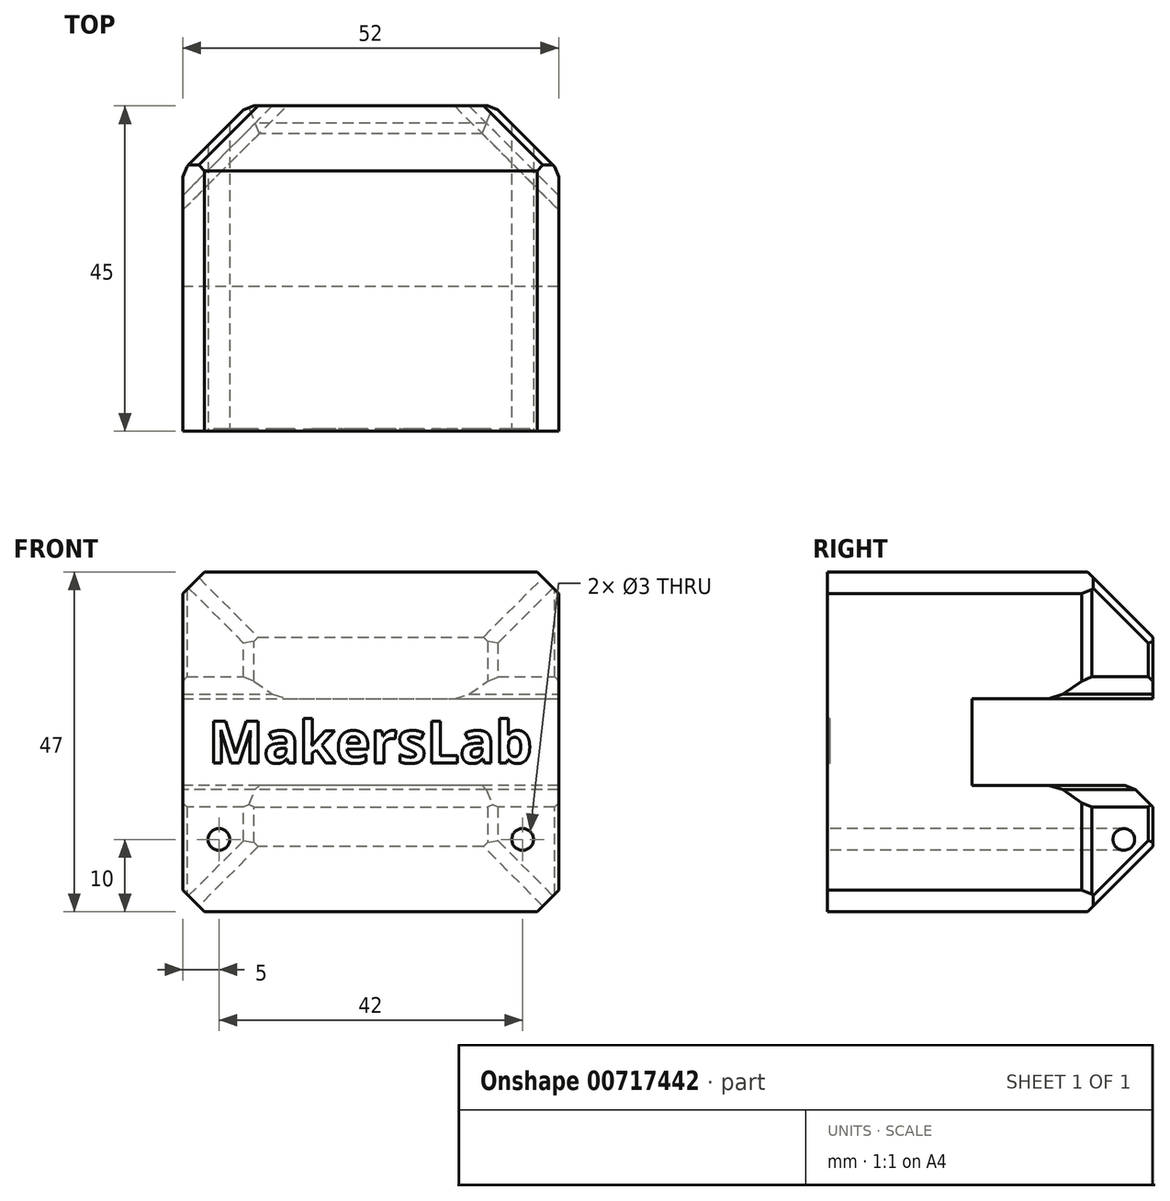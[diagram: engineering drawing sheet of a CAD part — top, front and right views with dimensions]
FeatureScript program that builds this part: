
annotation { "Feature Type Name" : "Feature", "Feature Type Description" : "" }
export const myFeature = defineFeature(function(context is Context, id is Id, definition is map)
    precondition{}
    {
        {
            var Q0;
            Q0=qCreatedBy(makeId("Front.planeOp"),FACE);
            var sketch = newSketch(context, id + "F0", { "sketchPlane" : qUnion([Q0])});
            skLineSegment(sketch, "E0", {"start": v(0, 0) * mm, "end": v(52, 0) * mm});
            skLineSegment(sketch, "E1", {"start": v(52, 0) * mm, "end": v(52, 47) * mm});
            skLineSegment(sketch, "E2", {"start": v(52, 47) * mm, "end": v(0, 47) * mm});
            skLineSegment(sketch, "E3", {"start": v(0, 47) * mm, "end": v(0, 0) * mm});
            skSolve(sketch);
        }
        {
            var Q0;
            Q0=makeQuery(id+"F0.imprint","IMPRINT",FACE,{"disambiguationData":[TD([[makeQuery(id+"F0.imprint","IMPRINT",EDGE,{"derivedFrom":sQuery(id+"F0.wireOp",EDGE,"E0")}),1.0]])]});
            extrude(context, id + "F1", {"entities" : qUnion([Q0]), "depth" : 45 * mm, "offsetDistance" : 25 * mm});
        }
        {
            var Q0;
            Q0=makeQuery(id+"F1.opExtrude","CAP_FACE",FACE,{"disambiguationData":[OSD([sQuery(id+"F0.wireOp",EDGE,"E0"),sQuery(id+"F0.wireOp",EDGE,"E1"),sQuery(id+"F0.wireOp",EDGE,"E2"),sQuery(id+"F0.wireOp",EDGE,"E3")])],"isStart":false});
            var sketch = newSketch(context, id + "F2", { "sketchPlane" : qUnion([Q0])});
            skCircle(sketch, "E4", {"center": v(5, 10) * mm, "radius": 1.5 * mm});
            skCircle(sketch, "E5", {"center": v(47, 10) * mm, "radius": 1.5 * mm});
            skSolve(sketch);
        }
        {
            var Q0;
            Q0 = qSketchRegion(id + "F2", true);
            extrude(context, id + "F3", {"entities" : qUnion([Q0]), "operationType" : NewBodyOperationType.REMOVE, "oppositeDirection" : true, "depth" : 100 * mm, "offsetDistance" : 25 * mm});
        }
        {
            var Q0;
            Q0=makeQuery(id+"F1.opExtrude","CAP_EDGE",EDGE,{"disambiguationData":[OSD([sQuery(id+"F0.wireOp",EDGE,"E0")])],"isStart":true});
            var Q1;
            Q1=makeQuery(id+"F1.opExtrude","CAP_EDGE",EDGE,{"disambiguationData":[OSD([sQuery(id+"F0.wireOp",EDGE,"E2")])],"isStart":true});
            var Q2;
            Q2=makeQuery(id+"F1.opExtrude","CAP_EDGE",EDGE,{"disambiguationData":[OSD([sQuery(id+"F0.wireOp",EDGE,"E3")])],"isStart":true});
            var Q3;
            Q3=makeQuery(id+"F1.opExtrude","CAP_EDGE",EDGE,{"disambiguationData":[OSD([sQuery(id+"F0.wireOp",EDGE,"E1")])],"isStart":true});
            chamfer(context, id + "F4", {"entities" : qUnion([Q0, Q1, Q2, Q3]), "width" : 9 * mm, "tangentPropagation" : true});
        }
        {
            var Q0;
            Q0=makeQuery(id+"F1.opExtrude","CAP_FACE",FACE,{"disambiguationData":[OSD([sQuery(id+"F0.wireOp",EDGE,"E0"),sQuery(id+"F0.wireOp",EDGE,"E1"),sQuery(id+"F0.wireOp",EDGE,"E2"),sQuery(id+"F0.wireOp",EDGE,"E3")])],"isStart":true});
            var sketch = newSketch(context, id + "F5", { "sketchPlane" : qUnion([Q0])});
            skLineSegment(sketch, "E6", {"start": v(0, 23.5) * mm, "end": v(0, 29.5) * mm});
            skPoint(sketch, "E6.startSnap0", {"position": v(-9, 23.5) * mm});
            skLineSegment(sketch, "E7", {"start": v(0, 29.5) * mm, "end": v(-52, 29.5) * mm});
            skLineSegment(sketch, "E8", {"start": v(-52, 29.5) * mm, "end": v(-52, 17.5) * mm});
            skLineSegment(sketch, "E9", {"start": v(-52, 17.5) * mm, "end": v(0, 17.5) * mm});
            skLineSegment(sketch, "E10", {"start": v(0, 17.5) * mm, "end": v(0, 23.5) * mm});
            skSolve(sketch);
        }
        {
            var Q0;
            {var subQ0=sQuery(id+"F5.wireOp",EDGE,"E7");var subQ1=sQuery(id+"F0.wireOp",EDGE,"E3");var subQ2=sQuery(id+"F0.wireOp",EDGE,"E1");var subQ3=makeQuery(id+"F1.opExtrude","CAP_FACE",FACE,{"disambiguationData":[OSD([sQuery(id+"F0.wireOp",EDGE,"E0"),subQ2,sQuery(id+"F0.wireOp",EDGE,"E2"),subQ1])],"isStart":true});var subQ4=makeQuery(id+"F4.opChamfer","BLEND_EDGE",EDGE,{"blendedFrom":[makeQuery(id+"F1.opExtrude","CAP_EDGE",EDGE,{"disambiguationData":[OSD([subQ1])],"isStart":true}),subQ3],"blendedInto":[subQ3]});var subQ5=makeQuery(id+"F5.imprint","INTERSECT",VERTEX,{"derivedFrom":[subQ4,subQ0]});Q0=makeQuery(id+"F5.imprint","IMPRINT",FACE,{"disambiguationData":[TD([[makeQuery(id+"F5.imprint","IMPRINT",EDGE,{"disambiguationData":[TD([[subQ5,-1.0]])],"derivedFrom":subQ0}),1.0]])]});}
            var Q1;
            {var subQ6=sQuery(id+"F5.wireOp",EDGE,"E6");Q1=makeQuery(id+"F5.imprint","IMPRINT",FACE,{"disambiguationData":[TD([[makeQuery(id+"F5.imprint","IMPRINT",EDGE,{"derivedFrom":subQ6}),1.0]])]});}
            var Q2;
            {var subQ0=sQuery(id+"F5.wireOp",EDGE,"E8");Q2=makeQuery(id+"F5.imprint","IMPRINT",FACE,{"disambiguationData":[TD([[makeQuery(id+"F5.imprint","IMPRINT",EDGE,{"derivedFrom":subQ0}),1.0]])]});}
            extrude(context, id + "F6", {"entities" : qUnion([Q0, Q1, Q2]), "operationType" : NewBodyOperationType.REMOVE, "oppositeDirection" : true, "depth" : 25 * mm, "offsetDistance" : 25 * mm});
        }
        {
            var Q0;
            Q0=makeQuery(id+"F6.boolean.opBoolean","INTERSECT",EDGE,{"derivedFrom":[makeQuery(id+"F4.opChamfer","BLEND_FACE",FACE,{"disambiguationData":[OSD([sQuery(id+"F0.wireOp",EDGE,"E1")])]}),makeQuery(id+"F6.opExtrude","SWEPT_FACE",FACE,{"disambiguationData":[OSD([sQuery(id+"F5.wireOp",EDGE,"E7")])]})]});
            var Q1;
            Q1=makeQuery(id+"F6.boolean.opBoolean","COPY",EDGE,{"derivedFrom":makeQuery(id+"F6.opExtrude","CAP_EDGE",EDGE,{"disambiguationData":[OSD([sQuery(id+"F5.wireOp",EDGE,"E7")])],"isStart":true})});
            var Q2;
            Q2=makeQuery(id+"F6.boolean.opBoolean","INTERSECT",EDGE,{"derivedFrom":[makeQuery(id+"F4.opChamfer","BLEND_FACE",FACE,{"disambiguationData":[OSD([sQuery(id+"F0.wireOp",EDGE,"E3")])]}),makeQuery(id+"F6.opExtrude","SWEPT_FACE",FACE,{"disambiguationData":[OSD([sQuery(id+"F5.wireOp",EDGE,"E7")])]})]});
            var Q3;
            Q3=makeQuery(id+"F6.boolean.opBoolean","INTERSECT",EDGE,{"derivedFrom":[makeQuery(id+"F4.opChamfer","BLEND_FACE",FACE,{"disambiguationData":[OSD([sQuery(id+"F0.wireOp",EDGE,"E1")])]}),makeQuery(id+"F6.opExtrude","SWEPT_FACE",FACE,{"disambiguationData":[OSD([sQuery(id+"F5.wireOp",EDGE,"E9")])]})]});
            var Q4;
            Q4=makeQuery(id+"F6.boolean.opBoolean","COPY",EDGE,{"derivedFrom":makeQuery(id+"F6.opExtrude","CAP_EDGE",EDGE,{"disambiguationData":[OSD([sQuery(id+"F5.wireOp",EDGE,"E9")])],"isStart":true})});
            var Q5;
            Q5=makeQuery(id+"F6.boolean.opBoolean","INTERSECT",EDGE,{"derivedFrom":[makeQuery(id+"F4.opChamfer","BLEND_FACE",FACE,{"disambiguationData":[OSD([sQuery(id+"F0.wireOp",EDGE,"E3")])]}),makeQuery(id+"F6.opExtrude","SWEPT_FACE",FACE,{"disambiguationData":[OSD([sQuery(id+"F5.wireOp",EDGE,"E9")])]})]});
            var Q6;
            Q6=makeQuery(id+"F6.boolean.opBoolean","COPY",EDGE,{"derivedFrom":makeQuery(id+"F6.opExtrude","SWEPT_EDGE",EDGE,{"disambiguationData":[OSD([sQuery(id+"F5.wireOp",EDGE,"E7"),sQuery(id+"F5.wireOp",EDGE,"E8")])]})});
            var Q7;
            Q7=makeQuery(id+"F6.boolean.opBoolean","COPY",EDGE,{"derivedFrom":makeQuery(id+"F6.opExtrude","SWEPT_EDGE",EDGE,{"disambiguationData":[OSD([sQuery(id+"F5.wireOp",EDGE,"E8"),sQuery(id+"F5.wireOp",EDGE,"E9")])]})});
            var Q8;
            Q8=makeQuery(id+"F6.boolean.opBoolean","COPY",EDGE,{"derivedFrom":makeQuery(id+"F6.opExtrude","SWEPT_EDGE",EDGE,{"disambiguationData":[OSD([sQuery(id+"F5.wireOp",EDGE,"E6"),sQuery(id+"F5.wireOp",EDGE,"E7")])]})});
            var Q9;
            Q9=makeQuery(id+"F6.boolean.opBoolean","COPY",EDGE,{"derivedFrom":makeQuery(id+"F6.opExtrude","SWEPT_EDGE",EDGE,{"disambiguationData":[OSD([sQuery(id+"F5.wireOp",EDGE,"E9"),sQuery(id+"F5.wireOp",EDGE,"E10")])]})});
            chamfer(context, id + "F7", {"entities" : qUnion([Q0, Q1, Q2, Q3, Q4, Q5, Q6, Q7, Q8, Q9]), "width" : 3 * mm, "tangentPropagation" : true});
        }
        {
            var Q0;
            {var subQ0=sQuery(id+"F5.wireOp",EDGE,"E7");Q0=makeQuery(id+"F7.opChamfer","BLEND_EDGE",EDGE,{"blendedFrom":[makeQuery(id+"F6.boolean.opBoolean","COPY",EDGE,{"derivedFrom":makeQuery(id+"F6.opExtrude","SWEPT_EDGE",EDGE,{"disambiguationData":[OSD([sQuery(id+"F5.wireOp",EDGE,"E6"),subQ0])]})}),makeQuery(id+"F6.boolean.opBoolean","COPY",FACE,{"derivedFrom":makeQuery(id+"F6.opExtrude","SWEPT_FACE",FACE,{"disambiguationData":[OSD([subQ0])]})})],"blendedInto":[makeQuery(id+"F6.boolean.opBoolean","COPY",FACE,{"derivedFrom":makeQuery(id+"F6.opExtrude","SWEPT_FACE",FACE,{"disambiguationData":[OSD([subQ0])]})})]});}
            var Q1;
            {var subQ0=makeQuery(id+"F6.opExtrude","SWEPT_FACE",FACE,{"disambiguationData":[OSD([sQuery(id+"F5.wireOp",EDGE,"E7")])]});Q1=makeQuery(id+"F7.opChamfer","BLEND_EDGE",EDGE,{"blendedFrom":[makeQuery(id+"F6.boolean.opBoolean","INTERSECT",EDGE,{"derivedFrom":[makeQuery(id+"F4.opChamfer","BLEND_FACE",FACE,{"disambiguationData":[OSD([sQuery(id+"F0.wireOp",EDGE,"E3")])]}),subQ0]}),makeQuery(id+"F6.boolean.opBoolean","COPY",FACE,{"derivedFrom":subQ0})],"blendedInto":[makeQuery(id+"F6.boolean.opBoolean","COPY",FACE,{"derivedFrom":subQ0})]});}
            var Q2;
            {var subQ0=sQuery(id+"F5.wireOp",EDGE,"E7");Q2=makeQuery(id+"F7.opChamfer","BLEND_EDGE",EDGE,{"blendedFrom":[makeQuery(id+"F6.boolean.opBoolean","COPY",EDGE,{"derivedFrom":makeQuery(id+"F6.opExtrude","CAP_EDGE",EDGE,{"disambiguationData":[OSD([subQ0])],"isStart":true})}),makeQuery(id+"F6.boolean.opBoolean","COPY",FACE,{"derivedFrom":makeQuery(id+"F6.opExtrude","SWEPT_FACE",FACE,{"disambiguationData":[OSD([subQ0])]})})],"blendedInto":[makeQuery(id+"F6.boolean.opBoolean","COPY",FACE,{"derivedFrom":makeQuery(id+"F6.opExtrude","SWEPT_FACE",FACE,{"disambiguationData":[OSD([subQ0])]})})]});}
            var Q3;
            {var subQ0=makeQuery(id+"F6.opExtrude","SWEPT_FACE",FACE,{"disambiguationData":[OSD([sQuery(id+"F5.wireOp",EDGE,"E7")])]});Q3=makeQuery(id+"F7.opChamfer","BLEND_EDGE",EDGE,{"blendedFrom":[makeQuery(id+"F6.boolean.opBoolean","INTERSECT",EDGE,{"derivedFrom":[makeQuery(id+"F4.opChamfer","BLEND_FACE",FACE,{"disambiguationData":[OSD([sQuery(id+"F0.wireOp",EDGE,"E1")])]}),subQ0]}),makeQuery(id+"F6.boolean.opBoolean","COPY",FACE,{"derivedFrom":subQ0})],"blendedInto":[makeQuery(id+"F6.boolean.opBoolean","COPY",FACE,{"derivedFrom":subQ0})]});}
            var Q4;
            {var subQ0=sQuery(id+"F5.wireOp",EDGE,"E7");Q4=makeQuery(id+"F7.opChamfer","BLEND_EDGE",EDGE,{"blendedFrom":[makeQuery(id+"F6.boolean.opBoolean","COPY",EDGE,{"derivedFrom":makeQuery(id+"F6.opExtrude","SWEPT_EDGE",EDGE,{"disambiguationData":[OSD([subQ0,sQuery(id+"F5.wireOp",EDGE,"E8")])]})}),makeQuery(id+"F6.boolean.opBoolean","COPY",FACE,{"derivedFrom":makeQuery(id+"F6.opExtrude","SWEPT_FACE",FACE,{"disambiguationData":[OSD([subQ0])]})})],"blendedInto":[makeQuery(id+"F6.boolean.opBoolean","COPY",FACE,{"derivedFrom":makeQuery(id+"F6.opExtrude","SWEPT_FACE",FACE,{"disambiguationData":[OSD([subQ0])]})})]});}
            var Q5;
            {var subQ0=sQuery(id+"F5.wireOp",EDGE,"E9");Q5=makeQuery(id+"F7.opChamfer","BLEND_EDGE",EDGE,{"blendedFrom":[makeQuery(id+"F6.boolean.opBoolean","COPY",EDGE,{"derivedFrom":makeQuery(id+"F6.opExtrude","SWEPT_EDGE",EDGE,{"disambiguationData":[OSD([sQuery(id+"F5.wireOp",EDGE,"E8"),subQ0])]})}),makeQuery(id+"F6.boolean.opBoolean","COPY",FACE,{"derivedFrom":makeQuery(id+"F6.opExtrude","SWEPT_FACE",FACE,{"disambiguationData":[OSD([subQ0])]})})],"blendedInto":[makeQuery(id+"F6.boolean.opBoolean","COPY",FACE,{"derivedFrom":makeQuery(id+"F6.opExtrude","SWEPT_FACE",FACE,{"disambiguationData":[OSD([subQ0])]})})]});}
            var Q6;
            {var subQ0=makeQuery(id+"F6.opExtrude","SWEPT_FACE",FACE,{"disambiguationData":[OSD([sQuery(id+"F5.wireOp",EDGE,"E9")])]});Q6=makeQuery(id+"F7.opChamfer","BLEND_EDGE",EDGE,{"blendedFrom":[makeQuery(id+"F6.boolean.opBoolean","INTERSECT",EDGE,{"derivedFrom":[makeQuery(id+"F4.opChamfer","BLEND_FACE",FACE,{"disambiguationData":[OSD([sQuery(id+"F0.wireOp",EDGE,"E1")])]}),subQ0]}),makeQuery(id+"F6.boolean.opBoolean","COPY",FACE,{"derivedFrom":subQ0})],"blendedInto":[makeQuery(id+"F6.boolean.opBoolean","COPY",FACE,{"derivedFrom":subQ0})]});}
            var Q7;
            {var subQ0=sQuery(id+"F5.wireOp",EDGE,"E9");Q7=makeQuery(id+"F7.opChamfer","BLEND_EDGE",EDGE,{"blendedFrom":[makeQuery(id+"F6.boolean.opBoolean","COPY",EDGE,{"derivedFrom":makeQuery(id+"F6.opExtrude","CAP_EDGE",EDGE,{"disambiguationData":[OSD([subQ0])],"isStart":true})}),makeQuery(id+"F6.boolean.opBoolean","COPY",FACE,{"derivedFrom":makeQuery(id+"F6.opExtrude","SWEPT_FACE",FACE,{"disambiguationData":[OSD([subQ0])]})})],"blendedInto":[makeQuery(id+"F6.boolean.opBoolean","COPY",FACE,{"derivedFrom":makeQuery(id+"F6.opExtrude","SWEPT_FACE",FACE,{"disambiguationData":[OSD([subQ0])]})})]});}
            var Q8;
            {var subQ0=makeQuery(id+"F6.opExtrude","SWEPT_FACE",FACE,{"disambiguationData":[OSD([sQuery(id+"F5.wireOp",EDGE,"E9")])]});Q8=makeQuery(id+"F7.opChamfer","BLEND_EDGE",EDGE,{"blendedFrom":[makeQuery(id+"F6.boolean.opBoolean","INTERSECT",EDGE,{"derivedFrom":[makeQuery(id+"F4.opChamfer","BLEND_FACE",FACE,{"disambiguationData":[OSD([sQuery(id+"F0.wireOp",EDGE,"E3")])]}),subQ0]}),makeQuery(id+"F6.boolean.opBoolean","COPY",FACE,{"derivedFrom":subQ0})],"blendedInto":[makeQuery(id+"F6.boolean.opBoolean","COPY",FACE,{"derivedFrom":subQ0})]});}
            var Q9;
            {var subQ0=sQuery(id+"F5.wireOp",EDGE,"E9");Q9=makeQuery(id+"F7.opChamfer","BLEND_EDGE",EDGE,{"blendedFrom":[makeQuery(id+"F6.boolean.opBoolean","COPY",EDGE,{"derivedFrom":makeQuery(id+"F6.opExtrude","SWEPT_EDGE",EDGE,{"disambiguationData":[OSD([subQ0,sQuery(id+"F5.wireOp",EDGE,"E10")])]})}),makeQuery(id+"F6.boolean.opBoolean","COPY",FACE,{"derivedFrom":makeQuery(id+"F6.opExtrude","SWEPT_FACE",FACE,{"disambiguationData":[OSD([subQ0])]})})],"blendedInto":[makeQuery(id+"F6.boolean.opBoolean","COPY",FACE,{"derivedFrom":makeQuery(id+"F6.opExtrude","SWEPT_FACE",FACE,{"disambiguationData":[OSD([subQ0])]})})]});}
            var Q10;
            {var subQ0=sQuery(id+"F0.wireOp",EDGE,"E1");var subQ1=makeQuery(id+"F1.opExtrude","SWEPT_FACE",FACE,{"disambiguationData":[OSD([subQ0])]});var subQ2=sQuery(id+"F0.wireOp",EDGE,"E0");Q10=makeQuery(id+"F6.boolean.opBoolean","SPLIT",EDGE,{"disambiguationData":[TD([makeQuery(id+"F1.opExtrude","SWEPT_FACE",FACE,{"disambiguationData":[OSD([subQ2])]})])],"derivedFrom":makeQuery(id+"F4.opChamfer","BLEND_EDGE",EDGE,{"blendedFrom":[makeQuery(id+"F1.opExtrude","CAP_EDGE",EDGE,{"disambiguationData":[OSD([subQ0])],"isStart":true}),subQ1],"blendedInto":[subQ1]})});}
            var Q11;
            {var subQ0=sQuery(id+"F0.wireOp",EDGE,"E2");var subQ1=sQuery(id+"F0.wireOp",EDGE,"E1");var subQ2=makeQuery(id+"F1.opExtrude","SWEPT_FACE",FACE,{"disambiguationData":[OSD([subQ1])]});Q11=makeQuery(id+"F6.boolean.opBoolean","SPLIT",EDGE,{"disambiguationData":[TD([makeQuery(id+"F1.opExtrude","SWEPT_FACE",FACE,{"disambiguationData":[OSD([subQ0])]})])],"derivedFrom":makeQuery(id+"F4.opChamfer","BLEND_EDGE",EDGE,{"blendedFrom":[makeQuery(id+"F1.opExtrude","CAP_EDGE",EDGE,{"disambiguationData":[OSD([subQ1])],"isStart":true}),subQ2],"blendedInto":[subQ2]})});}
            var Q12;
            {var subQ0=sQuery(id+"F0.wireOp",EDGE,"E2");var subQ1=sQuery(id+"F0.wireOp",EDGE,"E1");var subQ2=makeQuery(id+"F1.opExtrude","CAP_FACE",FACE,{"disambiguationData":[OSD([sQuery(id+"F0.wireOp",EDGE,"E0"),subQ1,subQ0,sQuery(id+"F0.wireOp",EDGE,"E3")])],"isStart":true});Q12=makeQuery(id+"F6.boolean.opBoolean","SPLIT",EDGE,{"disambiguationData":[TD([makeQuery(id+"F4.opChamfer","BLEND_FACE",FACE,{"disambiguationData":[OSD([subQ0])]})])],"derivedFrom":makeQuery(id+"F4.opChamfer","BLEND_EDGE",EDGE,{"blendedFrom":[makeQuery(id+"F1.opExtrude","CAP_EDGE",EDGE,{"disambiguationData":[OSD([subQ1])],"isStart":true}),subQ2],"blendedInto":[subQ2]})});}
            var Q13;
            {var subQ0=sQuery(id+"F0.wireOp",EDGE,"E3");var subQ1=sQuery(id+"F0.wireOp",EDGE,"E2");var subQ2=makeQuery(id+"F1.opExtrude","CAP_FACE",FACE,{"disambiguationData":[OSD([sQuery(id+"F0.wireOp",EDGE,"E0"),sQuery(id+"F0.wireOp",EDGE,"E1"),subQ1,subQ0])],"isStart":true});Q13=makeQuery(id+"F6.boolean.opBoolean","SPLIT",EDGE,{"disambiguationData":[TD([makeQuery(id+"F4.opChamfer","BLEND_FACE",FACE,{"disambiguationData":[OSD([subQ1])]})])],"derivedFrom":makeQuery(id+"F4.opChamfer","BLEND_EDGE",EDGE,{"blendedFrom":[makeQuery(id+"F1.opExtrude","CAP_EDGE",EDGE,{"disambiguationData":[OSD([subQ0])],"isStart":true}),subQ2],"blendedInto":[subQ2]})});}
            var Q14;
            {var subQ0=sQuery(id+"F0.wireOp",EDGE,"E1");var subQ1=sQuery(id+"F0.wireOp",EDGE,"E0");var subQ2=makeQuery(id+"F1.opExtrude","CAP_FACE",FACE,{"disambiguationData":[OSD([subQ1,subQ0,sQuery(id+"F0.wireOp",EDGE,"E2"),sQuery(id+"F0.wireOp",EDGE,"E3")])],"isStart":true});Q14=makeQuery(id+"F6.boolean.opBoolean","SPLIT",EDGE,{"disambiguationData":[TD([makeQuery(id+"F4.opChamfer","BLEND_FACE",FACE,{"disambiguationData":[OSD([subQ1])]})])],"derivedFrom":makeQuery(id+"F4.opChamfer","BLEND_EDGE",EDGE,{"blendedFrom":[makeQuery(id+"F1.opExtrude","CAP_EDGE",EDGE,{"disambiguationData":[OSD([subQ0])],"isStart":true}),subQ2],"blendedInto":[subQ2]})});}
            var Q15;
            {var subQ0=sQuery(id+"F0.wireOp",EDGE,"E3");var subQ1=sQuery(id+"F0.wireOp",EDGE,"E0");var subQ2=makeQuery(id+"F1.opExtrude","CAP_FACE",FACE,{"disambiguationData":[OSD([subQ1,sQuery(id+"F0.wireOp",EDGE,"E1"),sQuery(id+"F0.wireOp",EDGE,"E2"),subQ0])],"isStart":true});Q15=makeQuery(id+"F6.boolean.opBoolean","SPLIT",EDGE,{"disambiguationData":[TD([makeQuery(id+"F4.opChamfer","BLEND_FACE",FACE,{"disambiguationData":[OSD([subQ1])]})])],"derivedFrom":makeQuery(id+"F4.opChamfer","BLEND_EDGE",EDGE,{"blendedFrom":[makeQuery(id+"F1.opExtrude","CAP_EDGE",EDGE,{"disambiguationData":[OSD([subQ0])],"isStart":true}),subQ2],"blendedInto":[subQ2]})});}
            var Q16;
            {var subQ0=sQuery(id+"F0.wireOp",EDGE,"E3");var subQ1=sQuery(id+"F0.wireOp",EDGE,"E0");var subQ2=makeQuery(id+"F1.opExtrude","SWEPT_FACE",FACE,{"disambiguationData":[OSD([subQ0])]});Q16=makeQuery(id+"F6.boolean.opBoolean","SPLIT",EDGE,{"disambiguationData":[TD([makeQuery(id+"F1.opExtrude","SWEPT_FACE",FACE,{"disambiguationData":[OSD([subQ1])]})])],"derivedFrom":makeQuery(id+"F4.opChamfer","BLEND_EDGE",EDGE,{"blendedFrom":[makeQuery(id+"F1.opExtrude","CAP_EDGE",EDGE,{"disambiguationData":[OSD([subQ0])],"isStart":true}),subQ2],"blendedInto":[subQ2]})});}
            var Q17;
            {var subQ0=sQuery(id+"F0.wireOp",EDGE,"E3");var subQ1=sQuery(id+"F0.wireOp",EDGE,"E2");var subQ2=makeQuery(id+"F1.opExtrude","SWEPT_FACE",FACE,{"disambiguationData":[OSD([subQ0])]});Q17=makeQuery(id+"F6.boolean.opBoolean","SPLIT",EDGE,{"disambiguationData":[TD([makeQuery(id+"F1.opExtrude","SWEPT_FACE",FACE,{"disambiguationData":[OSD([subQ1])]})])],"derivedFrom":makeQuery(id+"F4.opChamfer","BLEND_EDGE",EDGE,{"blendedFrom":[makeQuery(id+"F1.opExtrude","CAP_EDGE",EDGE,{"disambiguationData":[OSD([subQ0])],"isStart":true}),subQ2],"blendedInto":[subQ2]})});}
            var Q18;
            Q18=makeQuery(id+"F4.opChamfer","BLEND_EDGE",EDGE,{"blendedFrom":[makeQuery(id+"F1.opExtrude","CAP_EDGE",EDGE,{"disambiguationData":[OSD([sQuery(id+"F0.wireOp",EDGE,"E0")])],"isStart":true}),makeQuery(id+"F1.opExtrude","CAP_EDGE",EDGE,{"disambiguationData":[OSD([sQuery(id+"F0.wireOp",EDGE,"E3")])],"isStart":true})],"blendedInto":[]});
            var Q19;
            Q19=makeQuery(id+"F4.opChamfer","BLEND_EDGE",EDGE,{"blendedFrom":[makeQuery(id+"F1.opExtrude","CAP_EDGE",EDGE,{"disambiguationData":[OSD([sQuery(id+"F0.wireOp",EDGE,"E0")])],"isStart":true}),makeQuery(id+"F1.opExtrude","CAP_EDGE",EDGE,{"disambiguationData":[OSD([sQuery(id+"F0.wireOp",EDGE,"E1")])],"isStart":true})],"blendedInto":[]});
            var Q20;
            Q20=makeQuery(id+"F4.opChamfer","BLEND_EDGE",EDGE,{"blendedFrom":[makeQuery(id+"F1.opExtrude","CAP_EDGE",EDGE,{"disambiguationData":[OSD([sQuery(id+"F0.wireOp",EDGE,"E1")])],"isStart":true}),makeQuery(id+"F1.opExtrude","CAP_EDGE",EDGE,{"disambiguationData":[OSD([sQuery(id+"F0.wireOp",EDGE,"E2")])],"isStart":true})],"blendedInto":[]});
            var Q21;
            Q21=makeQuery(id+"F4.opChamfer","BLEND_EDGE",EDGE,{"blendedFrom":[makeQuery(id+"F1.opExtrude","CAP_EDGE",EDGE,{"disambiguationData":[OSD([sQuery(id+"F0.wireOp",EDGE,"E2")])],"isStart":true}),makeQuery(id+"F1.opExtrude","CAP_EDGE",EDGE,{"disambiguationData":[OSD([sQuery(id+"F0.wireOp",EDGE,"E3")])],"isStart":true})],"blendedInto":[]});
            chamfer(context, id + "F8", {"entities" : qUnion([Q0, Q1, Q2, Q3, Q4, Q5, Q6, Q7, Q8, Q9, Q10, Q11, Q12, Q13, Q14, Q15, Q16, Q17, Q18, Q19, Q20, Q21]), "width" : 2 * mm, "tangentPropagation" : true});
        }
        {
            var Q0;
            Q0=makeQuery(id+"F1.opExtrude","SWEPT_EDGE",EDGE,{"disambiguationData":[OSD([sQuery(id+"F0.wireOp",EDGE,"E1"),sQuery(id+"F0.wireOp",EDGE,"E2")])]});
            var Q1;
            Q1=makeQuery(id+"F1.opExtrude","SWEPT_EDGE",EDGE,{"disambiguationData":[OSD([sQuery(id+"F0.wireOp",EDGE,"E0"),sQuery(id+"F0.wireOp",EDGE,"E1")])]});
            var Q2;
            Q2=makeQuery(id+"F1.opExtrude","SWEPT_EDGE",EDGE,{"disambiguationData":[OSD([sQuery(id+"F0.wireOp",EDGE,"E0"),sQuery(id+"F0.wireOp",EDGE,"E3")])]});
            var Q3;
            Q3=makeQuery(id+"F1.opExtrude","SWEPT_EDGE",EDGE,{"disambiguationData":[OSD([sQuery(id+"F0.wireOp",EDGE,"E2"),sQuery(id+"F0.wireOp",EDGE,"E3")])]});
            chamfer(context, id + "F9", {"entities" : qUnion([Q0, Q1, Q2, Q3]), "width" : 3 * mm, "tangentPropagation" : true});
        }
        {
            var Q0;
            Q0=makeQuery(id+"F1.opExtrude","CAP_FACE",FACE,{"disambiguationData":[OSD([sQuery(id+"F0.wireOp",EDGE,"E0"),sQuery(id+"F0.wireOp",EDGE,"E1"),sQuery(id+"F0.wireOp",EDGE,"E2"),sQuery(id+"F0.wireOp",EDGE,"E3")])],"isStart":false});
            var sketch = newSketch(context, id + "F10", { "sketchPlane" : qUnion([Q0])});
            skText(sketch, "E11", { "text": "MakersLab", "fontName": "OpenSans-Bold.ttf"});
            const initialGuessF10  = {"E11": [0.0035, 0.02057, 1, 0, 0.00586]};
            skSetInitialGuess(sketch, initialGuessF10);
            skSolve(sketch);
        }
        {
            var Q0;
            Q0 = qSketchRegion(id + "F10", true);
            extrude(context, id + "F11", {"entities" : qUnion([Q0]), "operationType" : NewBodyOperationType.REMOVE, "depth" : -0.3 * mm, "offsetDistance" : 25 * mm});
        }
    });
